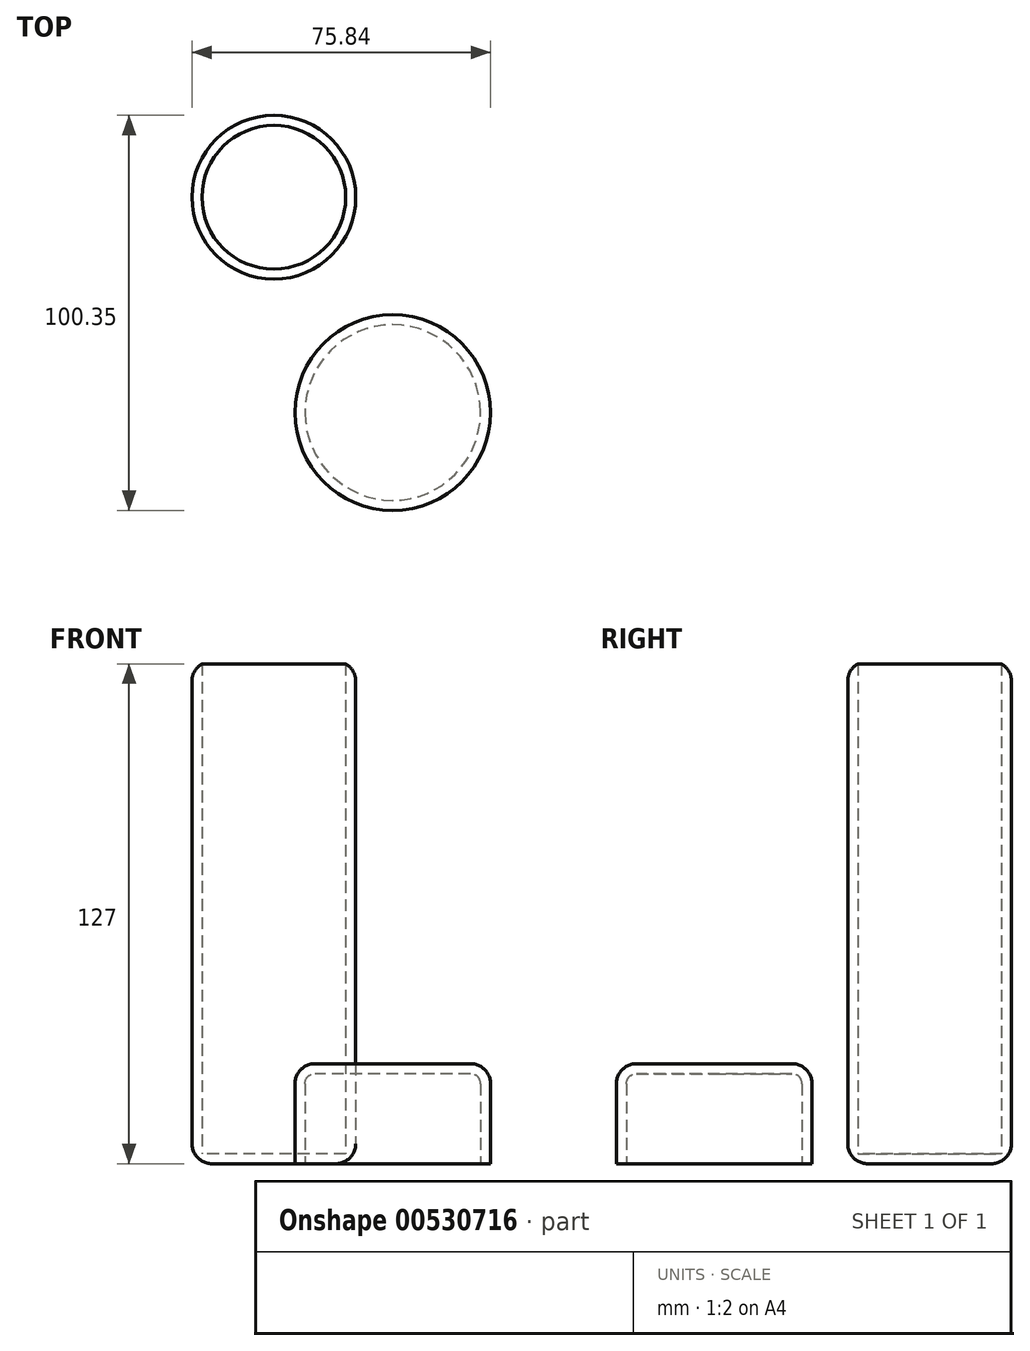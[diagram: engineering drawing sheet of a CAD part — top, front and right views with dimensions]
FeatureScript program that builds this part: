
annotation { "Feature Type Name" : "Feature", "Feature Type Description" : "" }
export const myFeature = defineFeature(function(context is Context, id is Id, definition is map)
    precondition{}
    {
        {
            var Q0;
            Q0=qCreatedBy(makeId("Top.planeOp"),FACE);
            var sketch = newSketch(context, id + "F0", { "sketchPlane" : qUnion([Q0])});
            skCircle(sketch, "E0", {"center": v(0, 0) * mm, "radius": 20.8 * mm});
            skSolve(sketch);
        }
        {
            var Q0;
            Q0=makeQuery(id+"F0.imprint","IMPRINT",FACE,{"disambiguationData":[TD([[makeQuery(id+"F0.imprint","IMPRINT",EDGE,{"derivedFrom":sQuery(id+"F0.wireOp",EDGE,"E0")}),1.0]])]});
            extrude(context, id + "F1", {"entities" : qUnion([Q0]), "depth" : 127 * mm, "offsetDistance" : 25.4 * mm});
        }
        {
            var Q0;
            Q0=makeQuery(id+"F1.opExtrude","CAP_FACE",FACE,{"disambiguationData":[OSD([sQuery(id+"F0.wireOp",EDGE,"E0")])],"isStart":false});
            shell(context, id + "F2", {"entities" : qUnion([Q0]), "thickness" : 2.54 * mm});
        }
        {
            var Q0;
            Q0=makeQuery(id+"F1.opExtrude","SWEPT_FACE",FACE,{"disambiguationData":[OSD([sQuery(id+"F0.wireOp",EDGE,"E0")])]});
            var Q1;
            Q1=makeQuery(id+"F1.opExtrude","CAP_EDGE",EDGE,{"disambiguationData":[OSD([sQuery(id+"F0.wireOp",EDGE,"E0")])],"isStart":true});
            fillet(context, id + "F3", {"entities" : qUnion([Q0, Q1]), "radius" : 5.08 * mm, "tangentPropagation" : true, "allowEdgeOverflow" : false});
        }
        {
            var Q0;
            Q0=qCreatedBy(makeId("Top.planeOp"),FACE);
            var sketch = newSketch(context, id + "F4", { "sketchPlane" : qUnion([Q0])});
            skCircle(sketch, "E1", {"center": v(30.2, -54.71) * mm, "radius": 24.84 * mm});
            skSolve(sketch);
        }
        {
            var Q0;
            Q0=makeQuery(id+"F4.imprint","IMPRINT",FACE,{"disambiguationData":[TD([[makeQuery(id+"F4.imprint","IMPRINT",EDGE,{"derivedFrom":sQuery(id+"F4.wireOp",EDGE,"E1")}),1.0]])]});
            extrude(context, id + "F5", {"entities" : qUnion([Q0]), "depth" : 25.4 * mm, "offsetDistance" : 25.4 * mm});
        }
        {
            var Q0;
            Q0=makeQuery(id+"F5.opExtrude","CAP_EDGE",EDGE,{"disambiguationData":[OSD([sQuery(id+"F4.wireOp",EDGE,"E1")])],"isStart":false});
            fillet(context, id + "F6", {"entities" : qUnion([Q0]), "radius" : 5.08 * mm, "tangentPropagation" : true, "allowEdgeOverflow" : false});
        }
        {
            var Q0;
            Q0=makeQuery(id+"F5.opExtrude","CAP_FACE",FACE,{"disambiguationData":[OSD([sQuery(id+"F4.wireOp",EDGE,"E1")])],"isStart":true});
            shell(context, id + "F7", {"entities" : qUnion([Q0]), "thickness" : 2.54 * mm});
        }
    });
